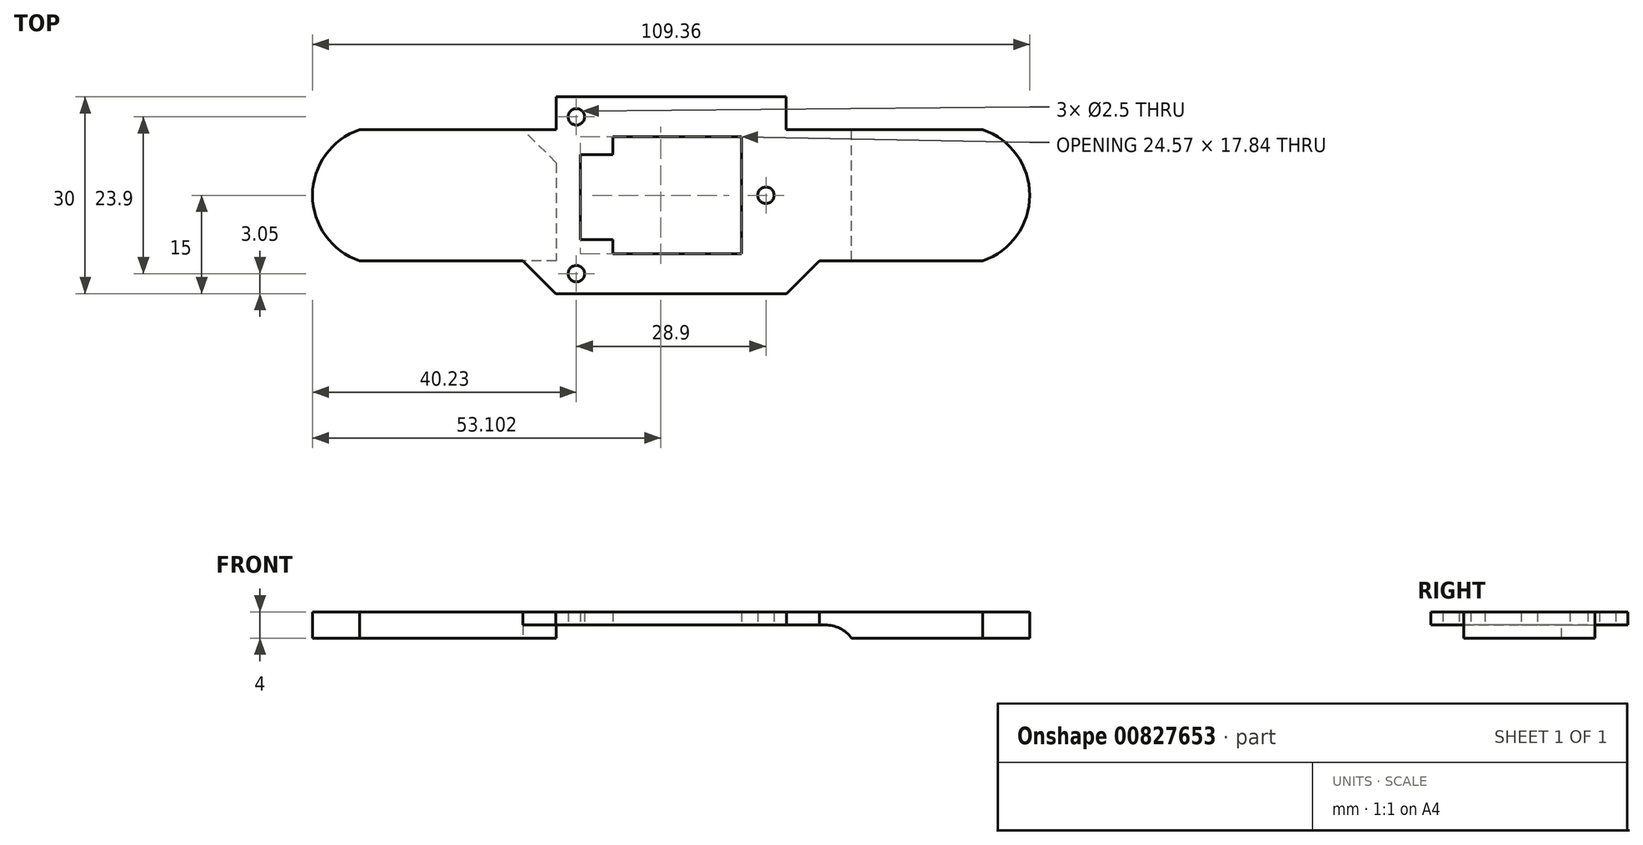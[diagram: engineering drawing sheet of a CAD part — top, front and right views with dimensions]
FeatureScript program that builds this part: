
annotation { "Feature Type Name" : "Feature", "Feature Type Description" : "" }
export const myFeature = defineFeature(function(context is Context, id is Id, definition is map)
    precondition{}
    {
        {
            var Q0;
            Q0=qCreatedBy(makeId("Top.planeOp"),FACE);
            var sketch = newSketch(context, id + "F0", { "sketchPlane" : qUnion([Q0])});
            skLineSegment(sketch, "E0.bottom", {"start": v(17.5, 15) * mm, "end": v(-17.5, 15) * mm});
            skLineSegment(sketch, "E0.top", {"start": v(17.5, -15) * mm, "end": v(-17.5, -15) * mm});
            skLineSegment(sketch, "E0.left", {"start": v(17.5, 15) * mm, "end": v(17.5, -15) * mm});
            skLineSegment(sketch, "E0.right", {"start": v(-17.5, 15) * mm, "end": v(-17.5, -15) * mm});
            skPoint(sketch, "E0.middle", {"position": v(0, 0) * mm});
            skCircle(sketch, "E1", {"center": v(-14.45, 11.95) * mm, "radius": 1.25 * mm});
            skCircle(sketch, "E2", {"center": v(-14.45, -11.95) * mm, "radius": 1.25 * mm});
            skCircle(sketch, "E3", {"center": v(14.45, 0) * mm, "radius": 1.25 * mm});
            skLineSegment(sketch, "E4.bottom", {"start": v(8.92, 8.92) * mm, "end": v(-8.92, 8.92) * mm});
            skLineSegment(sketch, "E4.top", {"start": v(8.92, -8.92) * mm, "end": v(-8.92, -8.92) * mm});
            skLineSegment(sketch, "E4.left", {"start": v(8.92, 8.92) * mm, "end": v(8.92, -8.92) * mm});
            skLineSegment(sketch, "E4.right", {"start": v(-8.92, 8.92) * mm, "end": v(-8.92, -8.92) * mm});
            skLineSegment(sketch, "E5", {"start": v(-8.92, 6.19) * mm, "end": v(-13.86, 6.19) * mm});
            skLineSegment(sketch, "E6", {"start": v(-13.86, 6.19) * mm, "end": v(-13.86, -6.78) * mm});
            skLineSegment(sketch, "E7", {"start": v(-13.86, -6.78) * mm, "end": v(-8.92, -6.78) * mm});
            skLineSegment(sketch, "E8", {"start": v(8.92, 8.92) * mm, "end": v(10.7, 8.92) * mm});
            skLineSegment(sketch, "E9", {"start": v(8.92, -8.92) * mm, "end": v(10.7, -8.92) * mm});
            skLineSegment(sketch, "E10", {"start": v(10.7, 8.92) * mm, "end": v(10.7, -8.92) * mm});
            skSolve(sketch);
        }
        {
            var Q0;
            Q0 = qSketchRegion(id + "F0", true);
            extrude(context, id + "F1", {"entities" : qUnion([Q0]), "depth" : 2 * mm, "offsetDistance" : 25.4 * mm});
        }
        {
            var Q0;
            Q0=makeQuery(id+"F1.opExtrude","CAP_FACE",FACE,{"disambiguationData":[OSD([sQuery(id+"F0.wireOp",EDGE,"E0.bottom"),sQuery(id+"F0.wireOp",EDGE,"E0.top"),sQuery(id+"F0.wireOp",EDGE,"E0.left"),sQuery(id+"F0.wireOp",EDGE,"E0.right"),sQuery(id+"F0.wireOp",EDGE,"E1"),sQuery(id+"F0.wireOp",EDGE,"E2"),sQuery(id+"F0.wireOp",EDGE,"E3"),sQuery(id+"F0.wireOp",EDGE,"E4.bottom"),sQuery(id+"F0.wireOp",EDGE,"E4.top"),sQuery(id+"F0.wireOp",EDGE,"E4.right"),sQuery(id+"F0.wireOp",EDGE,"E5"),sQuery(id+"F0.wireOp",EDGE,"E6"),sQuery(id+"F0.wireOp",EDGE,"E7"),sQuery(id+"F0.wireOp",EDGE,"E8"),sQuery(id+"F0.wireOp",EDGE,"E9"),sQuery(id+"F0.wireOp",EDGE,"E10")])],"isStart":false});
            var sketch = newSketch(context, id + "F2", { "sketchPlane" : qUnion([Q0])});
            skLineSegment(sketch, "E11.bottom", {"start": v(17.5, -10) * mm, "end": v(47.5, -10) * mm});
            skLineSegment(sketch, "E11.top", {"start": v(17.5, 10) * mm, "end": v(47.5, 10) * mm});
            skLineSegment(sketch, "E11.left", {"start": v(17.5, -10) * mm, "end": v(17.5, 10) * mm});
            skLineSegment(sketch, "E11.right", {"start": v(47.5, -10) * mm, "end": v(47.5, 10) * mm});
            skPoint(sketch, "E12.firstSnap0", {"position": v(0.9, -8.92) * mm});
            skLineSegment(sketch, "E12.bottom", {"start": v(-17.5, -10) * mm, "end": v(-47.5, -10) * mm});
            skLineSegment(sketch, "E12.top", {"start": v(-17.5, 10) * mm, "end": v(-47.5, 10) * mm});
            skLineSegment(sketch, "E12.left", {"start": v(-17.5, -10) * mm, "end": v(-17.5, 10) * mm});
            skLineSegment(sketch, "E12.right", {"start": v(-47.5, -10) * mm, "end": v(-47.5, 10) * mm});
            skArc(sketch, "E13", {"start": v(-47.5, 10) * mm, "mid": v(-54.68, 0) * mm, "end": v(-47.5, -10) * mm});
            skArc(sketch, "E14", {"start": v(47.5, -10) * mm, "mid": v(54.68, 0) * mm, "end": v(47.5, 10) * mm});
            skLineSegment(sketch, "E15", {"start": v(27.5, -10) * mm, "end": v(27.5, 10) * mm});
            skSolve(sketch);
        }
        {
            var Q0;
            Q0=makeQuery(id+"F2.imprint","IMPRINT",FACE,{"disambiguationData":[TD([[makeQuery(id+"F2.imprint","IMPRINT",EDGE,{"derivedFrom":sQuery(id+"F2.wireOp",EDGE,"E11.right")}),-1.0]])]});
            var Q1;
            Q1=makeQuery(id+"F2.imprint","IMPRINT",FACE,{"disambiguationData":[TD([[makeQuery(id+"F2.imprint","IMPRINT",EDGE,{"derivedFrom":sQuery(id+"F2.wireOp",EDGE,"E12.right")}),1.0]])]});
            var Q2;
            {var subQ1=sQuery(id+"F2.wireOp",EDGE,"E11.right");Q2=makeQuery(id+"F2.imprint","IMPRINT",FACE,{"disambiguationData":[TD([[makeQuery(id+"F2.imprint","IMPRINT",EDGE,{"derivedFrom":subQ1}),1.0]])]});}
            var Q3;
            Q3=makeQuery(id+"F2.imprint","IMPRINT",FACE,{"disambiguationData":[TD([[makeQuery(id+"F2.imprint","IMPRINT",EDGE,{"derivedFrom":sQuery(id+"F2.wireOp",EDGE,"E12.bottom")}),-1.0]])]});
            var Q4;
            {var subQ0=sQuery(id+"F2.wireOp",EDGE,"E11.left");Q4=makeQuery(id+"F2.imprint","IMPRINT",FACE,{"disambiguationData":[TD([[makeQuery(id+"F2.imprint","IMPRINT",EDGE,{"derivedFrom":subQ0}),1.0]])]});}
            extrude(context, id + "F3", {"entities" : qUnion([Q0, Q1, Q2, Q3, Q4]), "operationType" : NewBodyOperationType.ADD, "oppositeDirection" : true, "depth" : 4 * mm, "offsetDistance" : 25.4 * mm});
        }
        {
            var Q0;
            {var subQ0=sQuery(id+"F0.wireOp",EDGE,"E0.right");var subQ1=sQuery(id+"F2.wireOp",EDGE,"E12.top");Q0=makeQuery(id+"F3.boolean.opBoolean","SPLIT",EDGE,{"disambiguationData":[topologyDisambiguationEdgeConnected([makeQuery(id+"F1.opExtrude","SWEPT_FACE",FACE,{"disambiguationData":[OSD([subQ0])]})])],"derivedFrom":makeQuery(id+"F3.opExtrude","SWEPT_EDGE",EDGE,{"disambiguationData":[OSD([subQ0,subQ1,sQuery(id+"F2.wireOp",EDGE,"E12.left")])]})});}
            chamfer(context, id + "F4", {"entities" : qUnion([Q0]), "width" : 5.08 * mm, "tangentPropagation" : true});
        }
        {
            var Q0;
            {var subQ0=sQuery(id+"F0.wireOp",EDGE,"E0.right");var subQ1=sQuery(id+"F2.wireOp",EDGE,"E12.bottom");Q0=makeQuery(id+"F3.boolean.opBoolean","SPLIT",EDGE,{"disambiguationData":[topologyDisambiguationEdgeConnected([makeQuery(id+"F1.opExtrude","SWEPT_FACE",FACE,{"disambiguationData":[OSD([subQ0])]})])],"derivedFrom":makeQuery(id+"F3.opExtrude","SWEPT_EDGE",EDGE,{"disambiguationData":[OSD([subQ0,subQ1,sQuery(id+"F2.wireOp",EDGE,"E12.left")])]})});}
            chamfer(context, id + "F5", {"entities" : qUnion([Q0]), "width" : 5.08 * mm, "tangentPropagation" : true});
        }
        {
            var Q0;
            {var subQ0=sQuery(id+"F0.wireOp",EDGE,"E0.left");var subQ1=sQuery(id+"F2.wireOp",EDGE,"E11.bottom");Q0=makeQuery(id+"F3.boolean.opBoolean","SPLIT",EDGE,{"disambiguationData":[topologyDisambiguationEdgeConnected([makeQuery(id+"F1.opExtrude","SWEPT_FACE",FACE,{"disambiguationData":[OSD([subQ0])]})])],"derivedFrom":makeQuery(id+"F3.opExtrude","SWEPT_EDGE",EDGE,{"disambiguationData":[OSD([subQ0,subQ1,sQuery(id+"F2.wireOp",EDGE,"E11.left")])]})});}
            chamfer(context, id + "F6", {"entities" : qUnion([Q0]), "width" : 5.08 * mm, "tangentPropagation" : true});
        }
        {
            var Q0;
            {var subQ0=sQuery(id+"F0.wireOp",EDGE,"E0.left");var subQ1=sQuery(id+"F2.wireOp",EDGE,"E11.top");Q0=makeQuery(id+"F3.boolean.opBoolean","SPLIT",EDGE,{"disambiguationData":[topologyDisambiguationEdgeConnected([makeQuery(id+"F1.opExtrude","SWEPT_FACE",FACE,{"disambiguationData":[OSD([subQ0])]})])],"derivedFrom":makeQuery(id+"F3.opExtrude","SWEPT_EDGE",EDGE,{"disambiguationData":[OSD([subQ0,subQ1,sQuery(id+"F2.wireOp",EDGE,"E11.left")])]})});}
            chamfer(context, id + "F7", {"entities" : qUnion([Q0]), "width" : 5.08 * mm, "tangentPropagation" : true});
        }
        {
            var Q0;
            Q0=makeQuery(id+"F3.opExtrude","CAP_FACE",FACE,{"disambiguationData":[OSD([sQuery(id+"F2.wireOp",EDGE,"E11.bottom"),sQuery(id+"F2.wireOp",EDGE,"E11.top"),sQuery(id+"F2.wireOp",EDGE,"E11.left"),sQuery(id+"F2.wireOp",EDGE,"E14")])],"isStart":false});
            var sketch = newSketch(context, id + "F8", { "sketchPlane" : qUnion([Q0])});
            skLineSegment(sketch, "E16", {"start": v(27.5, 10) * mm, "end": v(27.5, -10) * mm});
            skSolve(sketch);
        }
        {
            var Q0;
            Q0 = qSketchRegion(id + "F8", true);
            var Q1;
            {var subQ0=sQuery(id+"F8.wireOp",EDGE,"E16");Q1=makeQuery(id+"F8.imprint","IMPRINT",FACE,{"disambiguationData":[TD([[makeQuery(id+"F8.imprint","IMPRINT",EDGE,{"derivedFrom":subQ0}),-1.0]])]});}
            extrude(context, id + "F9", {"entities" : qUnion([Q0, Q1]), "operationType" : NewBodyOperationType.REMOVE, "oppositeDirection" : true, "depth" : 2 * mm, "offsetDistance" : 25.4 * mm});
        }
        {
            var Q0;
            Q0=makeQuery(id+"F9.boolean.opBoolean","COPY",EDGE,{"derivedFrom":makeQuery(id+"F9.opExtrude","CAP_EDGE",EDGE,{"disambiguationData":[OSD([sQuery(id+"F8.wireOp",EDGE,"E16")])],"isStart":false})});
            fillet(context, id + "F10", {"entities" : qUnion([Q0]), "radius" : 5.08 * mm, "tangentPropagation" : true, "allowEdgeOverflow" : false});
        }
    });
